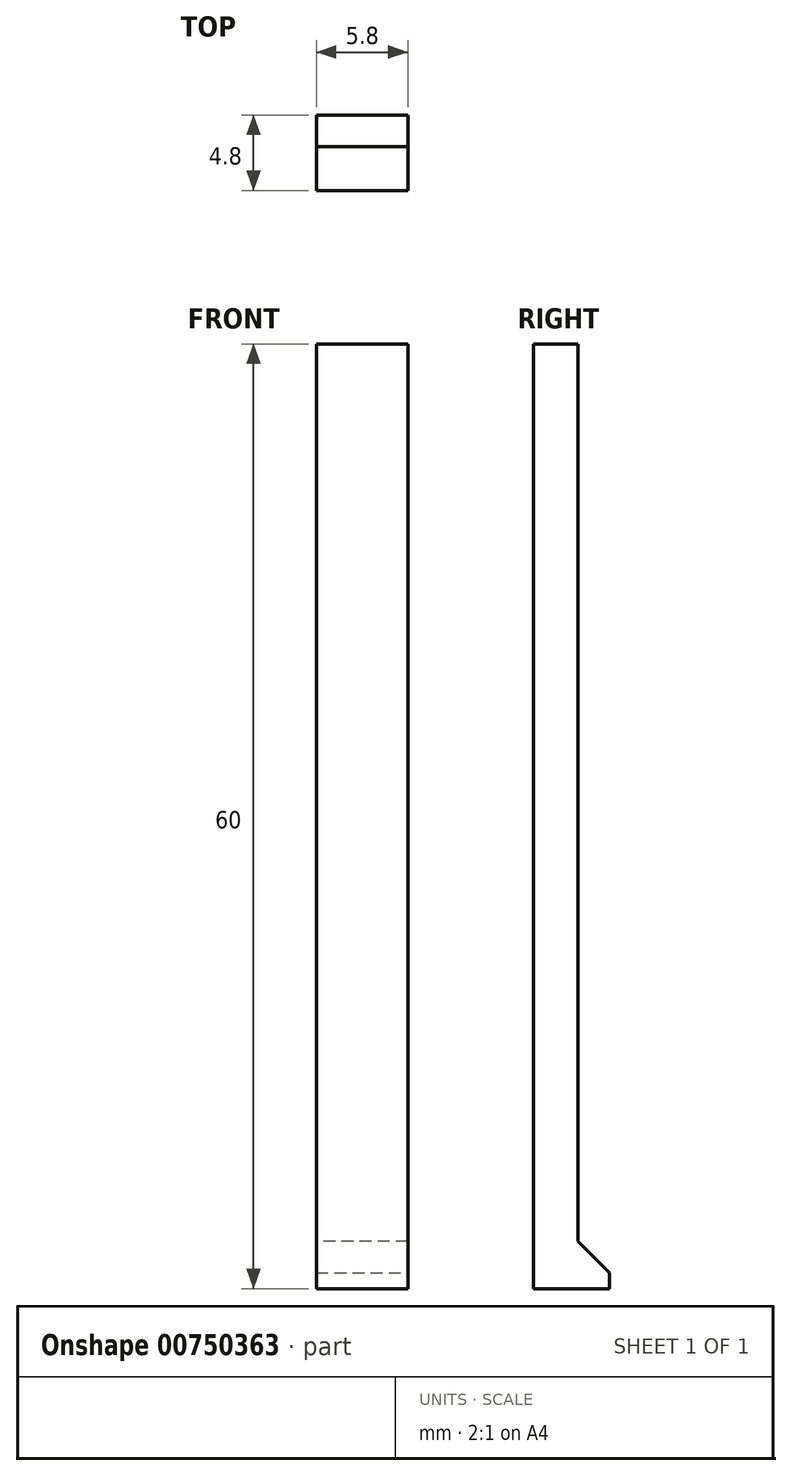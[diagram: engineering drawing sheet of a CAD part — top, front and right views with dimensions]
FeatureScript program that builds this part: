
annotation { "Feature Type Name" : "Feature", "Feature Type Description" : "" }
export const myFeature = defineFeature(function(context is Context, id is Id, definition is map)
    precondition{}
    {
        {
            var Q0;
            Q0=qCreatedBy(makeId("Top.planeOp"),FACE);
            var sketch = newSketch(context, id + "F0", { "sketchPlane" : qUnion([Q0])});
            skLineSegment(sketch, "E0.bottom", {"start": v(-17.76, 6.28) * mm, "end": v(-11.96, 6.28) * mm});
            skLineSegment(sketch, "E0.top", {"start": v(-17.76, 3.48) * mm, "end": v(-11.96, 3.48) * mm});
            skLineSegment(sketch, "E0.left", {"start": v(-17.76, 6.28) * mm, "end": v(-17.76, 3.48) * mm});
            skLineSegment(sketch, "E0.right", {"start": v(-11.96, 6.28) * mm, "end": v(-11.96, 3.48) * mm});
            skLineSegment(sketch, "E1.0", {"start": v(-19.76, 8.28) * mm, "end": v(-9.96, 8.28) * mm});
            skLineSegment(sketch, "E2", {"start": v(-17.76, 3.48) * mm, "end": v(-19.76, 3.48) * mm});
            skLineSegment(sketch, "E3", {"start": v(-11.96, 3.48) * mm, "end": v(-9.96, 3.48) * mm});
            skLineSegment(sketch, "E4", {"start": v(-17.76, 6.28) * mm, "end": v(-17.76, 8.62) * mm});
            skLineSegment(sketch, "E5", {"start": v(-11.96, 6.28) * mm, "end": v(-11.96, 8.62) * mm});
            skSolve(sketch);
        }
        {
            var Q0;
            Q0 = qSketchRegion(id + "F0", true);
            extrude(context, id + "F1", {"entities" : qUnion([Q0]), "depth" : 3 * mm, "offsetDistance" : 25 * mm});
        }
        {
            var Q0;
            Q0=makeQuery(id+"F0.imprint","IMPRINT",FACE,{"disambiguationData":[TD([[makeQuery(id+"F0.imprint","IMPRINT",EDGE,{"derivedFrom":sQuery(id+"F0.wireOp",EDGE,"E0.bottom")}),-1.0]])]});
            extrude(context, id + "F2", {"entities" : qUnion([Q0]), "operationType" : NewBodyOperationType.ADD, "depth" : 60 * mm, "offsetDistance" : 25 * mm});
        }
        {
            var Q0;
            Q0=makeQuery(id+"F1.opExtrude","CAP_EDGE",EDGE,{"disambiguationData":[OSD([sQuery(id+"F0.wireOp",EDGE,"E1.0")])],"isStart":false});
            var Q1;
            Q1=makeQuery(id+"F1.opExtrude","CAP_EDGE",EDGE,{"disambiguationData":[OSD([sQuery(id+"F0.wireOp",EDGE,"E1.3")])],"isStart":false});
            var Q2;
            Q2=makeQuery(id+"F1.opExtrude","CAP_EDGE",EDGE,{"disambiguationData":[OSD([sQuery(id+"F0.wireOp",EDGE,"E1.1")])],"isStart":false});
            chamfer(context, id + "F3", {"entities" : qUnion([Q0, Q1, Q2]), "width" : 2 * mm, "tangentPropagation" : true});
        }
    });
